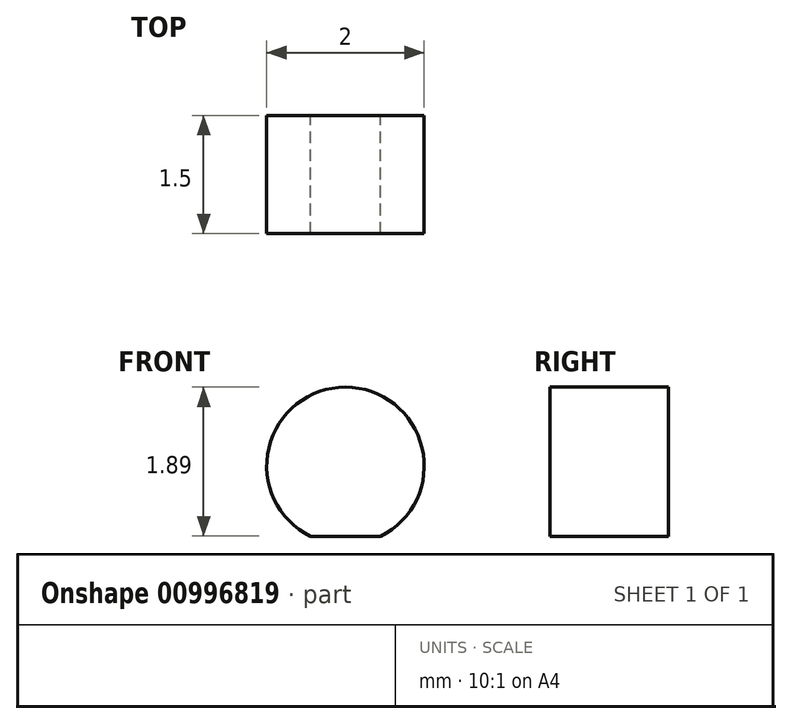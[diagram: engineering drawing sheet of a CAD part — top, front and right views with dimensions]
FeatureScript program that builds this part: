
annotation { "Feature Type Name" : "Feature", "Feature Type Description" : "" }
export const myFeature = defineFeature(function(context is Context, id is Id, definition is map)
    precondition{}
    {
        {
            var Q0;
            Q0=qCreatedBy(makeId("Front.planeOp"),FACE);
            var sketch = newSketch(context, id + "F0", { "sketchPlane" : qUnion([Q0])});
            skArc(sketch, "E0", {"start": v(0.45, -0.9) * mm, "mid": v(0, 1) * mm, "end": v(-0.45, -0.9) * mm});
            skLineSegment(sketch, "E1", {"start": v(-0.45, -0.9) * mm, "end": v(0.45, -0.9) * mm});
            skSolve(sketch);
        }
        {
            var Q0;
            Q0=makeQuery(id+"F0.imprint","IMPRINT",FACE,{"disambiguationData":[TD([[makeQuery(id+"F0.imprint","IMPRINT",EDGE,{"derivedFrom":sQuery(id+"F0.wireOp",EDGE,"E0")}),1.0]])]});
            extrude(context, id + "F1", {"entities" : qUnion([Q0]), "depth" : 1.5 * mm, "offsetDistance" : 25 * mm});
        }
    });
